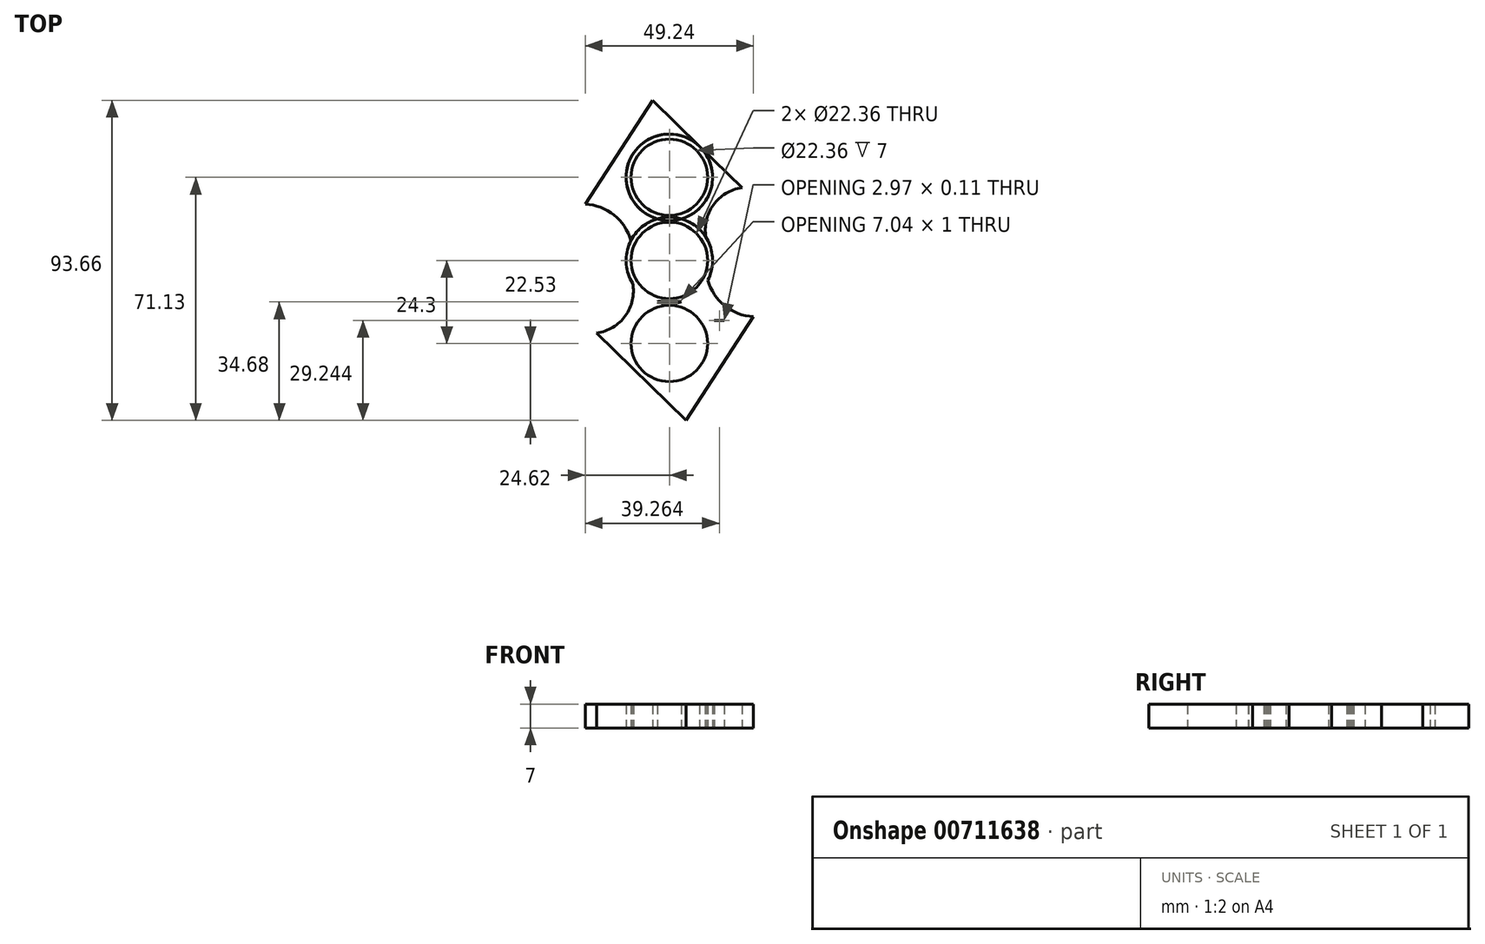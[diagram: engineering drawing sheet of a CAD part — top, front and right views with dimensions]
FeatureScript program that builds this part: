
annotation { "Feature Type Name" : "Feature", "Feature Type Description" : "" }
export const myFeature = defineFeature(function(context is Context, id is Id, definition is map)
    precondition{}
    {
        {
            var Q0;
            Q0=qCreatedBy(makeId("Top.planeOp"),FACE);
            var sketch = newSketch(context, id + "F0", { "sketchPlane" : qUnion([Q0])});
            skCircle(sketch, "E0", {"center": v(0, 0) * mm, "radius": 11.18 * mm});
            skCircle(sketch, "E1", {"center": v(0, 24.3) * mm, "radius": 11.18 * mm});
            skCircle(sketch, "E2", {"center": v(0, -24.3) * mm, "radius": 11.18 * mm});
            skCircle(sketch, "E3", {"center": v(0, 0) * mm, "radius": 12.65 * mm});
            skArc(sketch, "E4", {"start": v(3.52, -12.15) * mm, "mid": v(-2.7, -11.94) * mm, "end": v(-8.26, -14.72) * mm});
            skLineSegment(sketch, "E5", {"start": v(-4.94, 46.83) * mm, "end": v(18.15, 24.24) * mm});
            skLineSegment(sketch, "E6.1.0", {"start": v(16.13, -17.53) * mm, "end": v(4.94, -46.83) * mm});
            skLineSegment(sketch, "E6.1.1", {"start": v(4.94, -46.83) * mm, "end": v(-18.15, -24.24) * mm});
            skLineSegment(sketch, "E6.1.2", {"start": v(-18.15, -24.24) * mm, "end": v(-10.96, -17.3) * mm});
            skPoint(sketch, "E7.orphan", {"position": v(-18.04, 12.51) * mm});
            skArc(sketch, "E8.1.0", {"start": v(10.2, -16.8) * mm, "mid": v(13.12, -17.53) * mm, "end": v(16.13, -17.53) * mm});
            skPoint(sketch, "E9.orphan", {"position": v(18.04, -12.51) * mm});
            skPoint(sketch, "E10.orphan", {"position": v(5.05, 11.6) * mm});
            skArc(sketch, "E11.1.0", {"start": v(-10.96, -17.3) * mm, "mid": v(-8.09, -14.43) * mm, "end": v(-7.03, -10.51) * mm});
            skPoint(sketch, "E12.orphan", {"position": v(-5.05, -11.6) * mm});
            skArc(sketch, "E13.trimOffspring", {"start": v(-10.17, -16.78) * mm, "mid": v(-0.02, -36.95) * mm, "end": v(10.2, -16.8) * mm});
            skArc(sketch, "E14", {"start": v(5.04, -11.6) * mm, "mid": v(9.61, -16.39) * mm, "end": v(16.13, -17.53) * mm});
            skPoint(sketch, "E15.orphan", {"position": v(4.59, -12.51) * mm});
            skPoint(sketch, "E16.orphan", {"position": v(-4.59, 12.51) * mm});
            skLineSegment(sketch, "E17", {"start": v(-4.94, 46.83) * mm, "end": v(-24.62, 16.46) * mm});
            skArc(sketch, "E18", {"start": v(-11.26, 5.77) * mm, "mid": v(-16.21, 13.27) * mm, "end": v(-24.62, 16.46) * mm});
            skLineSegment(sketch, "E19", {"start": v(-4.94, 46.83) * mm, "end": v(21.2, 21.25) * mm});
            skArc(sketch, "E20", {"start": v(21.2, 21.25) * mm, "mid": v(12.86, 16.2) * mm, "end": v(10.74, 6.7) * mm});
            skPoint(sketch, "E21.orphan", {"position": v(10.96, 17.3) * mm});
            skLineSegment(sketch, "E22.1.0", {"start": v(4.94, -46.83) * mm, "end": v(24.62, -16.46) * mm});
            skArc(sketch, "E22.1.1", {"start": v(11.26, -5.77) * mm, "mid": v(16.21, -13.27) * mm, "end": v(24.62, -16.46) * mm});
            skArc(sketch, "E22.1.2", {"start": v(-21.2, -21.25) * mm, "mid": v(-12.86, -16.2) * mm, "end": v(-10.74, -6.7) * mm});
            skLineSegment(sketch, "E23", {"start": v(-21.2, -21.25) * mm, "end": v(-18.15, -24.24) * mm});
            skCircle(sketch, "E24", {"center": v(0, 24.3) * mm, "radius": 12.65 * mm});
            skSolve(sketch);
        }
        {
            var Q0;
            Q0=makeQuery(id+"F0.imprint","IMPRINT",FACE,{"disambiguationData":[TD([[makeQuery(id+"F0.imprint","IMPRINT",EDGE,{"derivedFrom":sQuery(id+"F0.wireOp",EDGE,"E1")}),-1.0]])]});
            var Q1;
            {var subQ0=sQuery(id+"F0.wireOp",EDGE,"E5");var subQ1=sQuery(id+"F0.wireOp",EDGE,"eTJealc5-xOxH-0BTB-Q50G-m7RXUDcQMioI");var subQ2=makeQuery(id+"F0.imprint","INTERSECT",VERTEX,{"derivedFrom":[subQ1,subQ0]});Q1=makeQuery(id+"F0.imprint","IMPRINT",FACE,{"disambiguationData":[TD([[makeQuery(id+"F0.imprint","IMPRINT",EDGE,{"disambiguationData":[TD([[subQ2,1.0]])],"derivedFrom":subQ1}),-1.0]])]});}
            var Q2;
            {var subQ0=sQuery(id+"F0.wireOp",EDGE,"526C52Gd-L9ob-C1Q6-Aa6H-I6RLuXwrUeDr");var subQ1=sQuery(id+"F0.wireOp",EDGE,"eTJealc5-xOxH-0BTB-Q50G-m7RXUDcQMioI");var subQ2=makeQuery(id+"F0.imprint","INTERSECT",VERTEX,{"derivedFrom":[subQ1,subQ0]});Q2=makeQuery(id+"F0.imprint","IMPRINT",FACE,{"disambiguationData":[TD([[makeQuery(id+"F0.imprint","IMPRINT",EDGE,{"disambiguationData":[TD([[subQ2,-1.0]])],"derivedFrom":subQ1}),-1.0]])]});}
            var Q3;
            {var subQ0=sQuery(id+"F0.wireOp",EDGE,"88J4eLKz-cB1z-D5jA-r6OH-GXoVl1bk7Pjf");Q3=makeQuery(id+"F0.imprint","IMPRINT",FACE,{"disambiguationData":[TD([[makeQuery(id+"F0.imprint","IMPRINT",EDGE,{"derivedFrom":subQ0}),-1.0]])]});}
            var Q4;
            {var subQ0=sQuery(id+"F0.wireOp",EDGE,"v3oPXUMJ-J7dK-oyDB-5Sgw-wjjaA9GnNe3E");var subQ1=sQuery(id+"F0.wireOp",EDGE,"E3");var subQ2=makeQuery(id+"F0.imprint","INTERSECT",VERTEX,{"disambiguationData":[OD(0.0)],"derivedFrom":[subQ1,subQ0]});Q4=makeQuery(id+"F0.imprint","IMPRINT",FACE,{"disambiguationData":[TD([[makeQuery(id+"F0.imprint","IMPRINT",EDGE,{"disambiguationData":[TD([[subQ2,-1.0]])],"derivedFrom":subQ1}),1.0]])]});}
            var Q5;
            {var subQ0=sQuery(id+"F0.wireOp",EDGE,"6fba0052-0d29-4d0e-af43-b5da28cb152a.1.0");Q5=makeQuery(id+"F0.imprint","IMPRINT",FACE,{"disambiguationData":[TD([[makeQuery(id+"F0.imprint","IMPRINT",EDGE,{"derivedFrom":subQ0}),-1.0]])]});}
            var Q6;
            {var subQ0=sQuery(id+"F0.wireOp",EDGE,"5quDzre1-KN5g-4J8S-71vg-aRWWjeghjOvG");var subQ1=sQuery(id+"F0.wireOp",EDGE,"E3");var subQ2=makeQuery(id+"F0.imprint","INTERSECT",VERTEX,{"derivedFrom":[subQ1,subQ0]});Q6=makeQuery(id+"F0.imprint","IMPRINT",FACE,{"disambiguationData":[TD([[makeQuery(id+"F0.imprint","IMPRINT",EDGE,{"disambiguationData":[TD([[subQ2,-1.0]])],"derivedFrom":subQ1}),-1.0]])]});}
            var Q7;
            Q7=makeQuery(id+"F0.imprint","IMPRINT",FACE,{"disambiguationData":[TD([[makeQuery(id+"F0.imprint","IMPRINT",EDGE,{"derivedFrom":sQuery(id+"F0.wireOp",EDGE,"E0")}),-1.0]])]});
            var Q8;
            {var subQ0=sQuery(id+"F0.wireOp",EDGE,"mGsnpPkv-33nn-kQA0-8lJQ-uJbSMW2OD3no");Q8=makeQuery(id+"F0.imprint","IMPRINT",FACE,{"disambiguationData":[TD([[makeQuery(id+"F0.imprint","IMPRINT",EDGE,{"derivedFrom":subQ0}),-1.0]])]});}
            var Q9;
            {var subQ0=sQuery(id+"F0.wireOp",EDGE,"E11.1.0");var subQ1=sQuery(id+"F0.wireOp",EDGE,"E3");var subQ2=makeQuery(id+"F0.imprint","INTERSECT",VERTEX,{"derivedFrom":[subQ1,subQ0]});Q9=makeQuery(id+"F0.imprint","IMPRINT",FACE,{"disambiguationData":[TD([[makeQuery(id+"F0.imprint","IMPRINT",EDGE,{"disambiguationData":[TD([[subQ2,-1.0]])],"derivedFrom":subQ1}),-1.0]])]});}
            var Q10;
            {var subQ0=sQuery(id+"F0.wireOp",EDGE,"E4");var subQ1=sQuery(id+"F0.wireOp",EDGE,"E3");var subQ2=makeQuery(id+"F0.imprint","INTERSECT",VERTEX,{"disambiguationData":[OD(0.0)],"derivedFrom":[subQ1,subQ0]});Q10=makeQuery(id+"F0.imprint","IMPRINT",FACE,{"disambiguationData":[TD([[makeQuery(id+"F0.imprint","IMPRINT",EDGE,{"disambiguationData":[TD([[subQ2,-1.0]])],"derivedFrom":subQ1}),1.0]])]});}
            var Q11;
            Q11=makeQuery(id+"F0.imprint","IMPRINT",FACE,{"disambiguationData":[TD([[makeQuery(id+"F0.imprint","IMPRINT",EDGE,{"derivedFrom":sQuery(id+"F0.wireOp",EDGE,"E2")}),-1.0]])]});
            var Q12;
            {var subQ0=sQuery(id+"F0.wireOp",EDGE,"E8.1.0");var subQ1=sQuery(id+"F0.wireOp",EDGE,"E6.1.0");var subQ2=makeQuery(id+"F0.imprint","INTERSECT",VERTEX,{"derivedFrom":[subQ1,subQ0]});Q12=makeQuery(id+"F0.imprint","IMPRINT",FACE,{"disambiguationData":[TD([[makeQuery(id+"F0.imprint","IMPRINT",EDGE,{"disambiguationData":[TD([[subQ2,-1.0]])],"derivedFrom":subQ1}),-1.0]])]});}
            var Q13;
            {var subQ0=sQuery(id+"F0.wireOp",EDGE,"E6.1.1");var subQ1=sQuery(id+"F0.wireOp",EDGE,"E6.1.0");var subQ2=makeQuery(id+"F0.imprint","INTERSECT",VERTEX,{"derivedFrom":[subQ1,subQ0]});Q13=makeQuery(id+"F0.imprint","IMPRINT",FACE,{"disambiguationData":[TD([[makeQuery(id+"F0.imprint","IMPRINT",EDGE,{"disambiguationData":[TD([[subQ2,1.0]])],"derivedFrom":subQ1}),-1.0]])]});}
            var Q14;
            {var subQ0=sQuery(id+"F0.wireOp",EDGE,"E6.1.2");Q14=makeQuery(id+"F0.imprint","IMPRINT",FACE,{"disambiguationData":[TD([[makeQuery(id+"F0.imprint","IMPRINT",EDGE,{"derivedFrom":subQ0}),-1.0]])]});}
            extrude(context, id + "F1", {"entities" : qUnion([Q0, Q1, Q2, Q3, Q4, Q5, Q6, Q7, Q8, Q9, Q10, Q11, Q12, Q13, Q14]), "depth" : 7 * mm, "offsetDistance" : 25 * mm});
        }
        {
            var Q0;
            {var subQ3=sQuery(id+"F0.wireOp",EDGE,"E6.1.2");Q0=makeQuery(id+"F0.imprint","IMPRINT",FACE,{"disambiguationData":[TD([[makeQuery(id+"F0.imprint","IMPRINT",EDGE,{"derivedFrom":subQ3}),1.0]])]});}
            var Q1;
            {var subQ8=sQuery(id+"F0.wireOp",EDGE,"E22.1.0");Q1=makeQuery(id+"F0.imprint","IMPRINT",FACE,{"disambiguationData":[TD([[makeQuery(id+"F0.imprint","IMPRINT",EDGE,{"derivedFrom":subQ8}),1.0]])]});}
            var Q2;
            {var subQ0=sQuery(id+"F0.wireOp",EDGE,"E6.1.1");var subQ3=sQuery(id+"F0.wireOp",EDGE,"E13.trimOffspring");var subQ5=makeQuery(id+"F0.imprint","INTERSECT",VERTEX,{"derivedFrom":[subQ3,subQ0]});Q2=makeQuery(id+"F0.imprint","IMPRINT",FACE,{"disambiguationData":[TD([[makeQuery(id+"F0.imprint","IMPRINT",EDGE,{"disambiguationData":[TD([[subQ5,-1.0]])],"derivedFrom":subQ3}),-1.0]])]});}
            extrude(context, id + "F2", {"entities" : qUnion([Q0, Q1, Q2]), "operationType" : NewBodyOperationType.ADD, "depth" : 7 * mm, "offsetDistance" : 25 * mm});
        }
        {
            var Q0;
            {var subQ1=sQuery(id+"F0.wireOp",EDGE,"E17");Q0=makeQuery(id+"F0.imprint","IMPRINT",FACE,{"disambiguationData":[TD([[makeQuery(id+"F0.imprint","IMPRINT",EDGE,{"derivedFrom":subQ1}),1.0]])]});}
            var Q1;
            {var subQ0=sQuery(id+"F0.wireOp",EDGE,"E20");Q1=makeQuery(id+"F0.imprint","IMPRINT",FACE,{"disambiguationData":[TD([[makeQuery(id+"F0.imprint","IMPRINT",EDGE,{"derivedFrom":subQ0}),-1.0]])]});}
            extrude(context, id + "F3", {"entities" : qUnion([Q0, Q1]), "depth" : 7 * mm, "offsetDistance" : 25 * mm});
        }
    });
